# Revit family: PUR52
name_source: partatom
category: Plumbing Fixtures
revit_build: Autodesk Revit 2015 (Build: 20140903_1530(x64)
units: mm (PartAtom-declared; Revit-internal decimal feet)

## types (6) — shared parameters
Aluminum = Aluminum
Chrome = Chrome
Glass = Glass
Manufacturer = SanSwiss
Model = PUR52
Seal = Seal
Type Comments = PUR
URL = http://www.sanswiss.com

## per-type parameters (varying)
| type | A - door | B | B - door | Connector | H | X |
| PUR52_6_800_350 | Door (A) : A=636 | 350 mm  [stored 1.14829 ft] | Door (B) : B=350 | Connector : A=636 | 453 mm | 800 mm  [stored 2.62467 ft] |
| PUR52_6_900_450 | Door (A) : A=636 | 450 mm  [stored 1.47638 ft] | Door (B) : B=450 | Connector : A=636 | 453 mm | 900 mm  [stored 2.95276 ft] |
| PUR52_6_1000_550 | Door (A) : A=636 | 550 mm | Door (B) : B=550 | Connector : A=636 | 453 mm | 1000 mm  [stored 3.28084 ft] |
| PUR52_7_800_300 | Door (A) : A=707 | 300 mm | Door (B) : B=300 | Connector : A=707 | 503 mm | 800 mm  [stored 2.62467 ft] |
| PUR52_7_900_400 | Door (A) : A=707 | 400 mm  [stored 1.31234 ft] | Door (B) : B=400 | Connector : A=707 | 503 mm | 900 mm  [stored 2.95276 ft] |
| PUR52_7_1000_500 | Door (A) : A=707 | 500 mm  [stored 1.64042 ft] | Door (B) : B=500 | Connector : A=707 | 503 mm | 1000 mm  [stored 3.28084 ft] |

note: [stored X ft] marks values corroborated as IEEE doubles in the binary element streams (Revit-internal decimal feet)

## geometry (parser evidence)
native form markers: Sweep x7
no freeform markers — native parametric forms only
